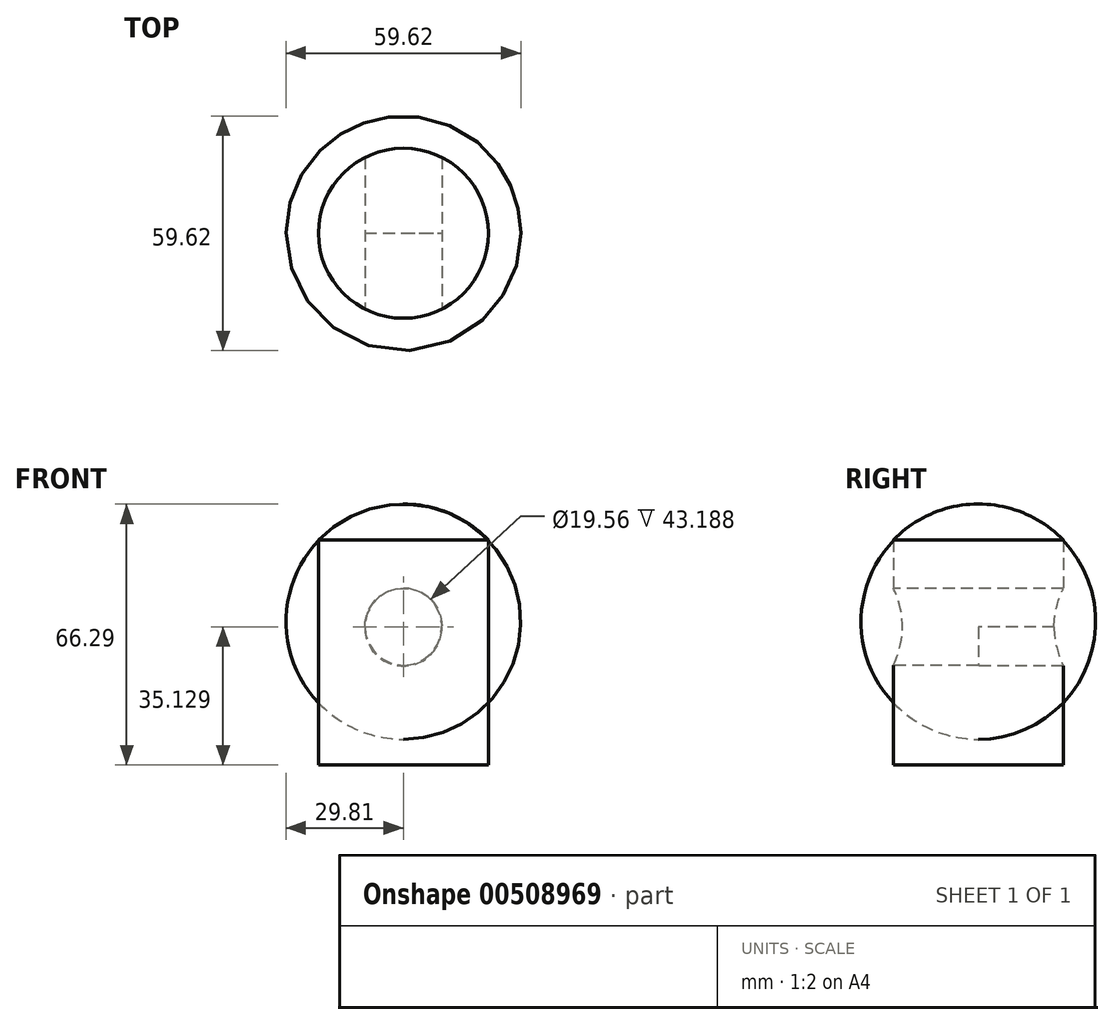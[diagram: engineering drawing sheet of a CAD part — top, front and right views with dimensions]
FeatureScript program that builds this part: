
annotation { "Feature Type Name" : "Feature", "Feature Type Description" : "" }
export const myFeature = defineFeature(function(context is Context, id is Id, definition is map)
    precondition{}
    {
        {
            var Q0;
            Q0=qCreatedBy(makeId("Front.planeOp"),FACE);
            var sketch = newSketch(context, id + "F0", { "sketchPlane" : qUnion([Q0])});
            skLineSegment(sketch, "E0", {"start": v(0, 0) * mm, "end": v(0, 66.3) * mm});
            skLineSegment(sketch, "E1", {"start": v(0, 0) * mm, "end": v(-21.6, 0) * mm});
            skLineSegment(sketch, "E2", {"start": v(-21.6, 0) * mm, "end": v(-21.6, 57.15) * mm});
            skArc(sketch, "E3", {"start": v(0, 66.3) * mm, "mid": v(-11.73, 63.93) * mm, "end": v(-21.6, 57.15) * mm});
            skSolve(sketch);
        }
        {
            var Q0;
            Q0=qSketchRegion(id+"F0",true);
            var Q1;
            Q1=sQuery(id+"F0.wireOp",EDGE,"E0");
            revolve(context, id + "F1", {"entities" : qUnion([Q0]), "axis" : qUnion([Q1]), "revolveType" : RevolveType.FULL});
        }
        {
            var Q0;
            Q0=qCreatedBy(makeId("Front.planeOp"),FACE);
            var sketch = newSketch(context, id + "F2", { "sketchPlane" : qUnion([Q0])});
            skLineSegment(sketch, "E4", {"start": v(0, 0) * mm, "end": v(0, 34.93) * mm});
            skCircle(sketch, "E5", {"center": v(0, 34.93) * mm, "radius": 9.78 * mm});
            skSolve(sketch);
        }
        {
            var Q0;
            Q0=qCreatedBy(makeId("Front.planeOp"),FACE);
            var sketch = newSketch(context, id + "F3", { "sketchPlane" : qUnion([Q0])});
            skLineSegment(sketch, "E6", {"start": v(0, 0) * mm, "end": v(0, 34.93) * mm});
            skCircle(sketch, "E7", {"center": v(0, 34.93) * mm, "radius": 9.78 * mm});
            skSolve(sketch);
        }
        {
            var Q0;
            Q0=qSketchRegion(id+"F3",true);
            extrude(context, id + "F4", {"entities" : qUnion([Q0]), "operationType" : NewBodyOperationType.REMOVE, "endBound" : BoundingType.THROUGH_ALL, "oppositeDirection" : true, "depth" : 25.4 * mm});
        }
        {
            var Q0;
            Q0=makeQuery(id+"F2.imprint","IMPRINT",FACE,{"disambiguationData":[TD([[makeQuery(id+"F2.imprint","IMPRINT",EDGE,{"derivedFrom":sQuery(id+"F2.wireOp",EDGE,"E5")}),1.0]])]});
            extrude(context, id + "F5", {"entities" : qUnion([Q0]), "operationType" : NewBodyOperationType.REMOVE, "endBound" : BoundingType.THROUGH_ALL, "oppositeDirection" : true, "depth" : 25.4 * mm});
        }
        {
            var Q0;
            Q0=qSketchRegion(id+"F3",true);
            extrude(context, id + "F6", {"entities" : qUnion([Q0]), "operationType" : NewBodyOperationType.REMOVE, "endBound" : BoundingType.THROUGH_ALL, "oppositeDirection" : true, "depth" : 25.4 * mm});
        }
        {
            var Q0;
            Q0=qSketchRegion(id+"F3",true);
            extrude(context, id + "F7", {"entities" : qUnion([Q0]), "operationType" : NewBodyOperationType.REMOVE, "endBound" : BoundingType.THROUGH_ALL, "oppositeDirection" : true, "depth" : 25.4 * mm});
        }
        {
            var Q0;
            Q0=qSketchRegion(id+"F3",true);
            extrude(context, id + "F8", {"entities" : qUnion([Q0]), "operationType" : NewBodyOperationType.REMOVE, "endBound" : BoundingType.THROUGH_ALL, "oppositeDirection" : true, "depth" : 25.4 * mm});
        }
        {
            var Q0;
            Q0=makeQuery(id+"F3.imprint","IMPRINT",FACE,{"disambiguationData":[TD([[makeQuery(id+"F3.imprint","IMPRINT",EDGE,{"derivedFrom":sQuery(id+"F3.wireOp",EDGE,"E7")}),1.0]])]});
            extrude(context, id + "F9", {"entities" : qUnion([Q0]), "operationType" : NewBodyOperationType.REMOVE, "endBound" : BoundingType.THROUGH_ALL, "oppositeDirection" : true, "depth" : 25.4 * mm});
        }
        {
            var Q0;
            Q0=qCreatedBy(makeId("Front.planeOp"),FACE);
            var sketch = newSketch(context, id + "F10", { "sketchPlane" : qUnion([Q0])});
            skLineSegment(sketch, "E8", {"start": v(0, 0) * mm, "end": v(0, 35.13) * mm});
            skCircle(sketch, "E9", {"center": v(0, 35.13) * mm, "radius": 9.78 * mm});
            skSolve(sketch);
        }
        {
            var Q0;
            Q0=qSketchRegion(id+"F3",true);
            extrude(context, id + "F11", {"entities" : qUnion([Q0]), "operationType" : NewBodyOperationType.REMOVE, "endBound" : BoundingType.THROUGH_ALL, "oppositeDirection" : true, "depth" : 25.4 * mm});
        }
        {
            var Q0;
            Q0=qSketchRegion(id+"F10",true);
            extrude(context, id + "F12", {"entities" : qUnion([Q0]), "operationType" : NewBodyOperationType.REMOVE, "endBound" : BoundingType.THROUGH_ALL, "oppositeDirection" : true, "depth" : 25.4 * mm, "hasSecondDirection" : true, "secondDirectionOppositeDirection" : false, "secondDirectionDepth" : 25.4 * mm});
        }
    });
